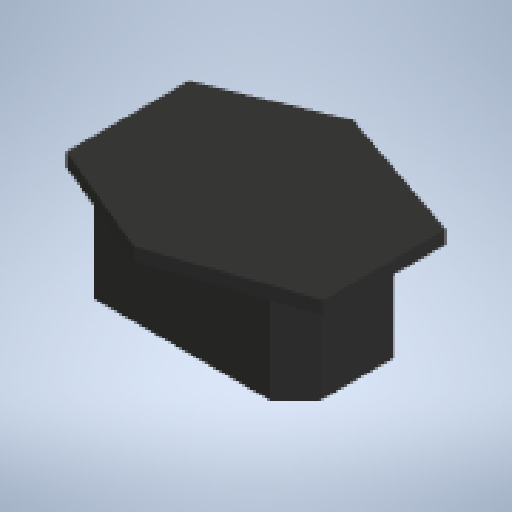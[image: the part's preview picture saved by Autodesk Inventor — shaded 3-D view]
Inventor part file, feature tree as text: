
AUTODESK INVENTOR PART (.ipt)
format: ipt  version: 2025 (Build 290162000, 162)  size: 245,248 bytes
history: native  units: in
note: dims shown in document units (in); Inventor stores cm internally (conversion verified against a paired STEP export)
features: extrude x2, sketch x2, projected_geometry x1
ambient origin geometry x8: Origin, YZ Plane, XZ Plane, XY Plane, X Axis, Y Axis, Z Axis, Center Point
bodies: Solid1 (feature_tree)
feature tree (5):
  extrude  "Extrusion1"  Depth=1.1024in
  extrude  "Extrusion2"  Depth=0.1181in
  sketch  "Sketch1"  dims[d1=1.1024in d3=0.315in]
  sketch  "Sketch2"  dims[d5=0.1969in d6=0.3937in d7=0.1969in d8=0.1969in d9=0.9in d10=0.0in d11=0.25in d12=0.25in d13=0.4331in d14=0.4331in d15=0.55in d16=1.1in d17=0.55in d18=1.1in d19=0.1181in d20=0.0in]
  projected_geometry  "Projected Loop1"
